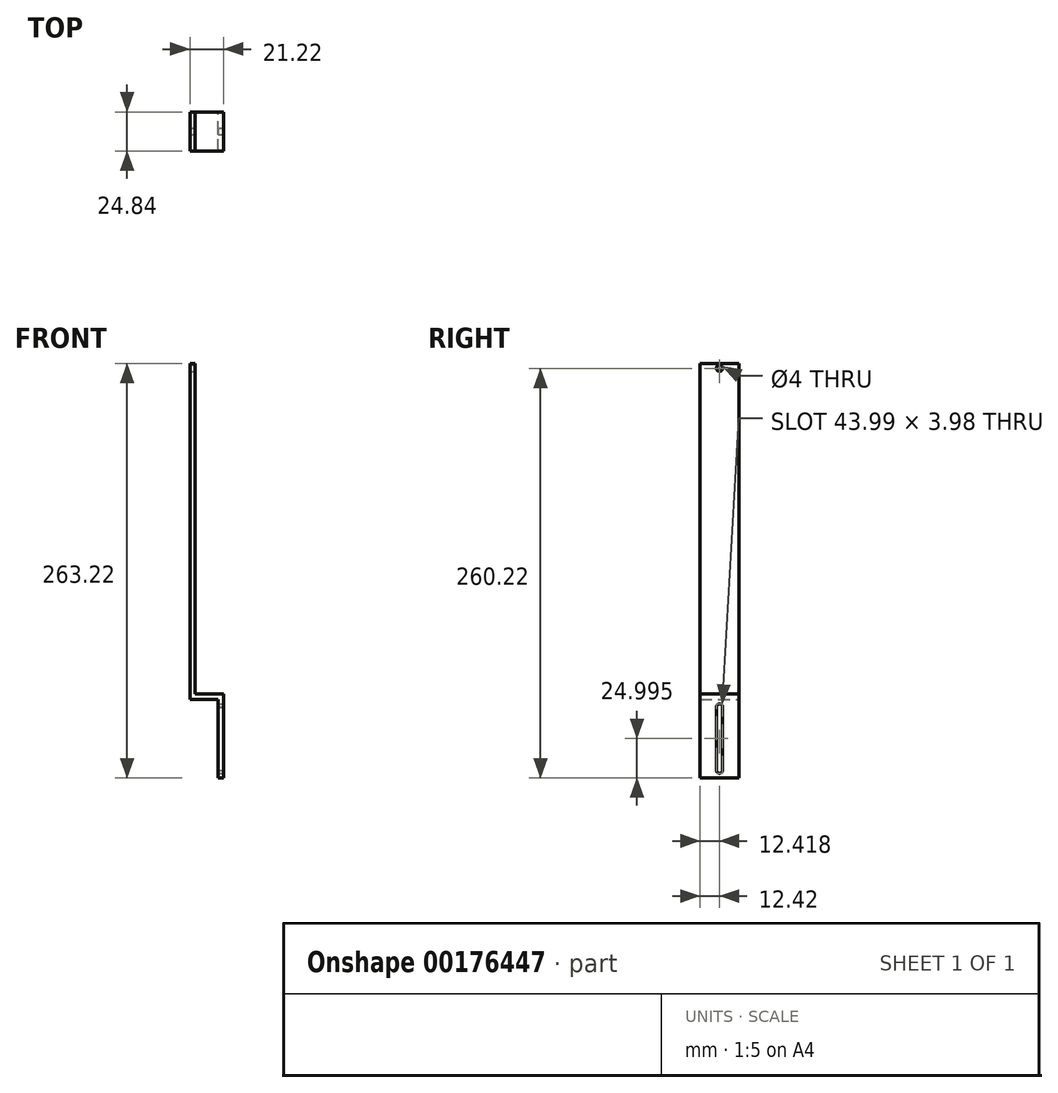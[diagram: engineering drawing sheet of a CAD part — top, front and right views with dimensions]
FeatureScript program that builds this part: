
annotation { "Feature Type Name" : "Feature", "Feature Type Description" : "" }
export const myFeature = defineFeature(function(context is Context, id is Id, definition is map)
    precondition{}
    {
        {
            var Q0;
            Q0=qCreatedBy(makeId("Top.planeOp"),FACE);
            var sketch = newSketch(context, id + "F0", { "sketchPlane" : qUnion([Q0])});
            skLineSegment(sketch, "E0.bottom", {"start": v(1.6, -12.42) * mm, "end": v(-1.61, -12.42) * mm});
            skLineSegment(sketch, "E0.top", {"start": v(1.6, 12.41) * mm, "end": v(-1.61, 12.41) * mm});
            skLineSegment(sketch, "E0.left", {"start": v(1.6, -12.42) * mm, "end": v(1.6, 12.41) * mm});
            skLineSegment(sketch, "E0.right", {"start": v(-1.61, -12.42) * mm, "end": v(-1.61, 12.41) * mm});
            skPoint(sketch, "E0.middle", {"position": v(0, 0) * mm});
            skSolve(sketch);
        }
        {
            var Q0;
            Q0=makeQuery(id+"F0.imprint","IMPRINT",FACE,{"disambiguationData":[TD([[makeQuery(id+"F0.imprint","IMPRINT",EDGE,{"derivedFrom":sQuery(id+"F0.wireOp",EDGE,"E0.bottom")}),-1.0]])]});
            extrude(context, id + "F1", {"entities" : qUnion([Q0]), "depth" : 3.22 * mm});
        }
        {
            var Q0;
            Q0=makeQuery(id+"F1.opExtrude","CAP_FACE",FACE,{"disambiguationData":[OSD([sQuery(id+"F0.wireOp",EDGE,"E0.bottom"),sQuery(id+"F0.wireOp",EDGE,"E0.top"),sQuery(id+"F0.wireOp",EDGE,"E0.left"),sQuery(id+"F0.wireOp",EDGE,"E0.right")])],"isStart":false});
            extrude(context, id + "F2", {"entities" : qUnion([Q0]), "operationType" : NewBodyOperationType.ADD, "depth" : 210 * mm});
        }
        {
            var Q0;
            {var subQ0=sQuery(id+"F0.wireOp",EDGE,"E0.left");Q0=makeQuery(id+"F2.boolean.opBoolean","MERGE",FACE,{"derivedFrom":[makeQuery(id+"F1.opExtrude","SWEPT_FACE",FACE,{"disambiguationData":[OSD([subQ0])]}),makeQuery(id+"F2.opExtrude","SWEPT_FACE",FACE,{"disambiguationData":[OSD([subQ0])]})]});}
            var sketch = newSketch(context, id + "F3", { "sketchPlane" : qUnion([Q0])});
            skCircle(sketch, "E1", {"center": v(0, 210.22) * mm, "radius": 2 * mm});
            skSolve(sketch);
        }
        {
            var Q0;
            Q0=sQuery(id+"F3.wireOp",VERTEX,"E1.center");
            var Q1;
            Q1=makeQuery(id+"F1.opExtrude","SWEPT_BODY",BODY,{"disambiguationData":[OSD([sQuery(id+"F0.wireOp",EDGE,"E0.bottom"),sQuery(id+"F0.wireOp",EDGE,"E0.top"),sQuery(id+"F0.wireOp",EDGE,"E0.left"),sQuery(id+"F0.wireOp",EDGE,"E0.right")])]});
            hole(context, id + "F4", {"style" : HoleStyle.SIMPLE, "endStyle" : HoleEndStyle.BLIND, "holeDiameter" : 4 * mm, "holeDepth" : 3.22 * mm, "startFromSketch" : true, "locations" : qUnion([Q0]), "scope" : qUnion([Q1])});
        }
        {
            var Q0;
            {var subQ0=sQuery(id+"F0.wireOp",EDGE,"E0.left");Q0=makeQuery(id+"F2.boolean.opBoolean","MERGE",FACE,{"derivedFrom":[makeQuery(id+"F1.opExtrude","SWEPT_FACE",FACE,{"disambiguationData":[OSD([subQ0])]}),makeQuery(id+"F2.opExtrude","SWEPT_FACE",FACE,{"disambiguationData":[OSD([subQ0])]})]});}
            var sketch = newSketch(context, id + "F5", { "sketchPlane" : qUnion([Q0])});
            skLineSegment(sketch, "E2", {"start": v(-12.42, 3.22) * mm, "end": v(12.41, 3.22) * mm});
            skSolve(sketch);
        }
        {
            var Q0;
            {var subQ0=sQuery(id+"F5.wireOp",EDGE,"E2");Q0=makeQuery(id+"F5.imprint","IMPRINT",FACE,{"disambiguationData":[TD([[makeQuery(id+"F5.imprint","IMPRINT",EDGE,{"derivedFrom":subQ0}),-1.0]])]});}
            extrude(context, id + "F6", {"entities" : qUnion([Q0]), "operationType" : NewBodyOperationType.ADD, "depth" : 18 * mm});
        }
        {
            var Q0;
            {var subQ0=sQuery(id+"F0.wireOp",EDGE,"E0.left");Q0=makeQuery(id+"F6.boolean.opBoolean","MERGE",FACE,{"derivedFrom":[makeQuery(id+"F1.opExtrude","CAP_FACE",FACE,{"disambiguationData":[OSD([sQuery(id+"F0.wireOp",EDGE,"E0.bottom"),sQuery(id+"F0.wireOp",EDGE,"E0.top"),subQ0,sQuery(id+"F0.wireOp",EDGE,"E0.right")])],"isStart":true}),makeQuery(id+"F6.opExtrude","SWEPT_FACE",FACE,{"disambiguationData":[OSD([subQ0])]})]});}
            var sketch = newSketch(context, id + "F7", { "sketchPlane" : qUnion([Q0])});
            skLineSegment(sketch, "E3", {"start": v(16.39, 12.42) * mm, "end": v(16.39, -12.42) * mm});
            skSolve(sketch);
        }
        {
            var Q0;
            {var subQ0=sQuery(id+"F7.wireOp",EDGE,"E3");Q0=makeQuery(id+"F7.imprint","IMPRINT",FACE,{"disambiguationData":[TD([[makeQuery(id+"F7.imprint","IMPRINT",EDGE,{"derivedFrom":subQ0}),1.0]])]});}
            extrude(context, id + "F8", {"entities" : qUnion([Q0]), "operationType" : NewBodyOperationType.ADD, "depth" : 50 * mm});
        }
        {
            var Q0;
            {var subQ0=sQuery(id+"F0.wireOp",EDGE,"E0.left");Q0=makeQuery(id+"F8.boolean.opBoolean","MERGE",FACE,{"derivedFrom":[makeQuery(id+"F6.opExtrude","CAP_FACE",FACE,{"disambiguationData":[OSD([sQuery(id+"F0.wireOp",EDGE,"E0.bottom"),sQuery(id+"F0.wireOp",EDGE,"E0.top"),subQ0,sQuery(id+"F5.wireOp",EDGE,"E2")])],"isStart":false}),makeQuery(id+"F8.opExtrude","SWEPT_FACE",FACE,{"disambiguationData":[OSD([subQ0])]})]});}
            var sketch = newSketch(context, id + "F9", { "sketchPlane" : qUnion([Q0])});
            skArc(sketch, "E4", {"start": v(1.99, -5.23) * mm, "mid": v(0.02, -3) * mm, "end": v(-2, -5.18) * mm});
            skArc(sketch, "E5", {"start": v(-2, -44.82) * mm, "mid": v(0.02, -47) * mm, "end": v(1.99, -44.77) * mm});
            skLineSegment(sketch, "E6", {"start": v(-2, -4.82) * mm, "end": v(-2, -45.18) * mm});
            skLineSegment(sketch, "E7", {"start": v(1.99, -5.23) * mm, "end": v(1.99, -45.23) * mm});
            skSolve(sketch);
        }
        {
            var Q0;
            {var subQ1=sQuery(id+"F9.wireOp",EDGE,"E4");var subQ6=sQuery(id+"F9.wireOp",EDGE,"E7");var subQ9=makeQuery(id+"F9.imprint","INTERSECT",VERTEX,{"derivedFrom":[subQ1,subQ6]});Q0=makeQuery(id+"F9.imprint","IMPRINT",FACE,{"disambiguationData":[TD([[makeQuery(id+"F9.imprint","IMPRINT",EDGE,{"disambiguationData":[TD([[subQ9,-1.0]])],"derivedFrom":subQ1}),1.0]])]});}
            extrude(context, id + "F10", {"entities" : qUnion([Q0]), "operationType" : NewBodyOperationType.REMOVE, "oppositeDirection" : true, "depth" : 3.22 * mm});
        }
    });
